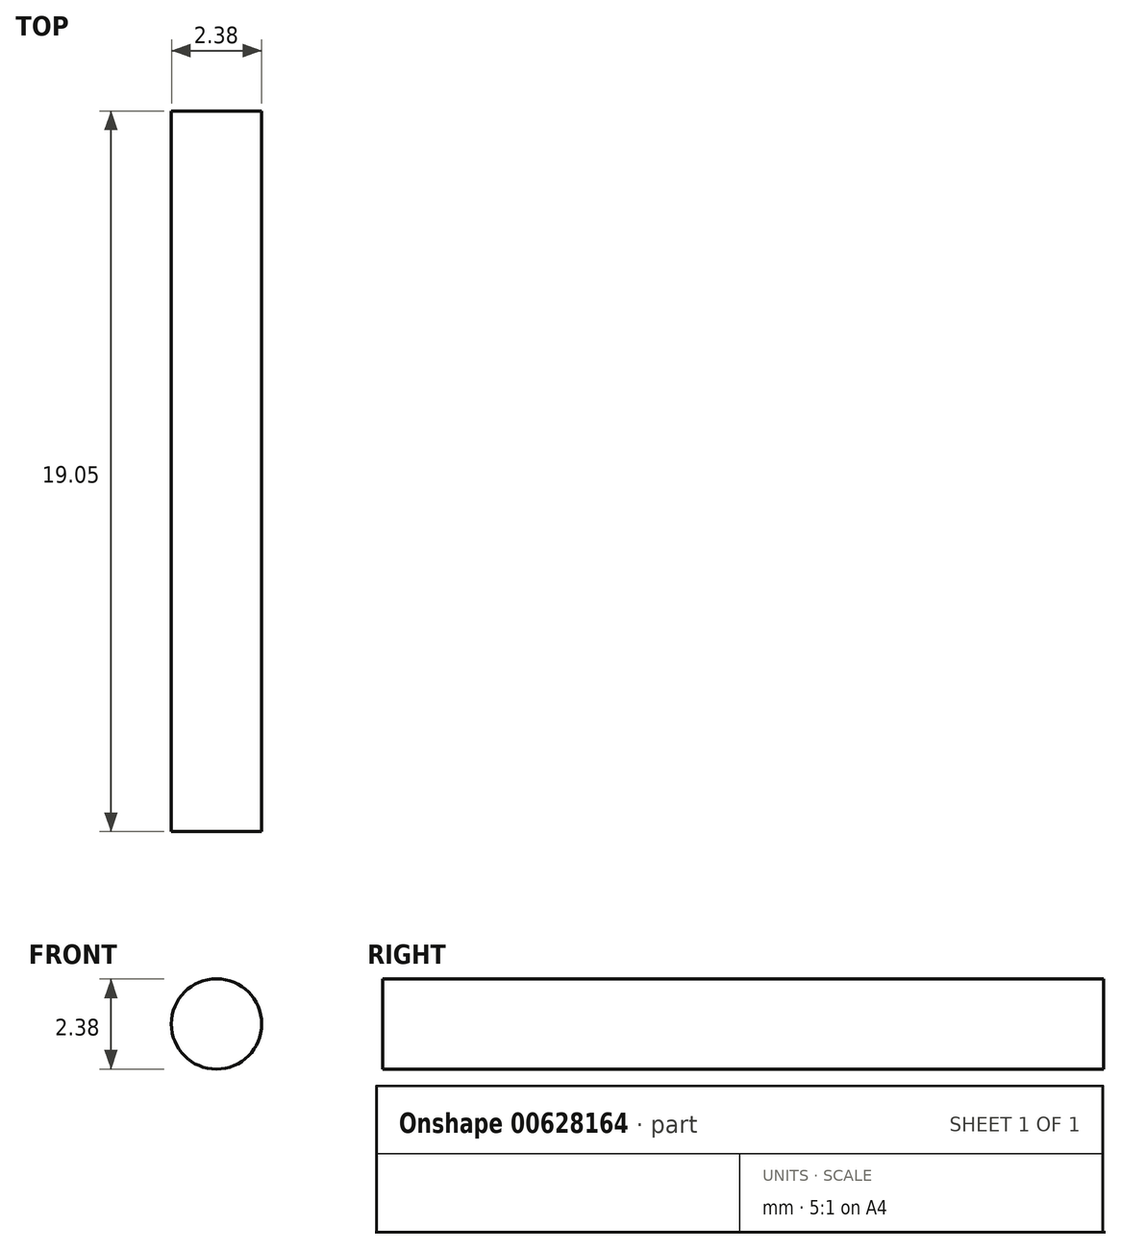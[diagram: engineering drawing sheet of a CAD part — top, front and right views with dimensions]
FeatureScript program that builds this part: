
annotation { "Feature Type Name" : "Feature", "Feature Type Description" : "" }
export const myFeature = defineFeature(function(context is Context, id is Id, definition is map)
    precondition{}
    {
        {
            var Q0;
            Q0=qCreatedBy(makeId("Front.planeOp"),FACE);
            var sketch = newSketch(context, id + "F0", { "sketchPlane" : qUnion([Q0])});
            skCircle(sketch, "E0", {"center": v(0, 0) * mm, "radius": 1.2 * mm});
            skSolve(sketch);
        }
        {
            var Q0;
            Q0=makeQuery(id+"F0.imprint","IMPRINT",FACE,{"disambiguationData":[TD([[makeQuery(id+"F0.imprint","IMPRINT",EDGE,{"derivedFrom":sQuery(id+"F0.wireOp",EDGE,"E0")}),1.0]])]});
            extrude(context, id + "F1", {"entities" : qUnion([Q0]), "depth" : 19.05 * mm, "offsetDistance" : 25.4 * mm});
        }
    });
